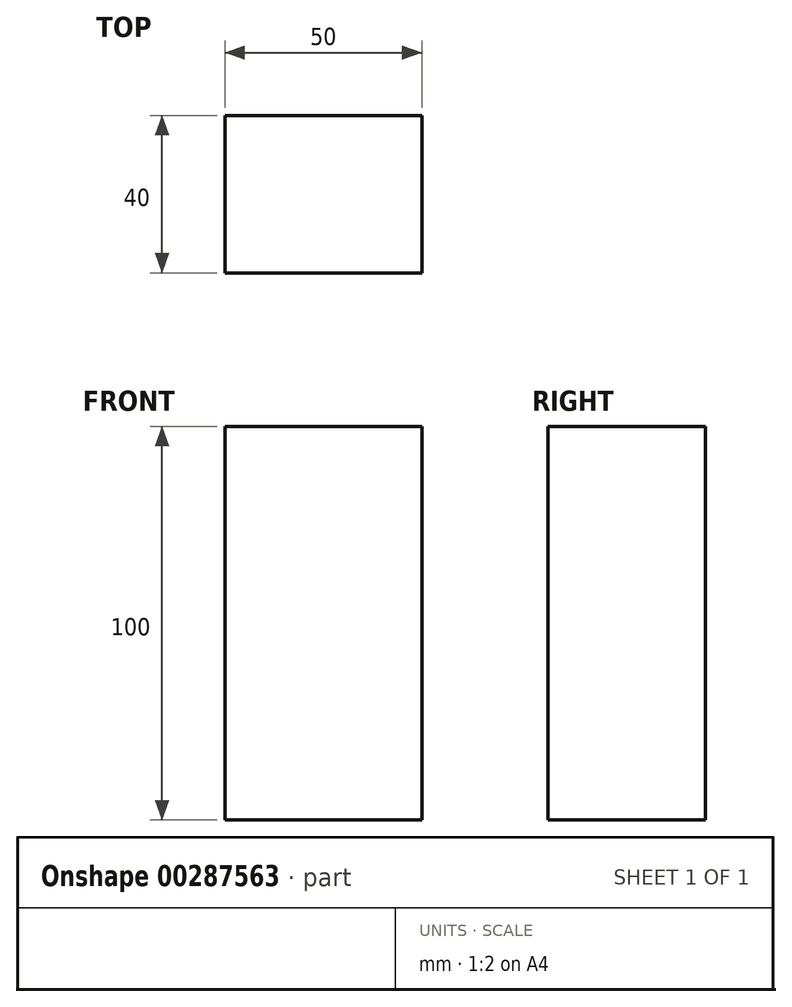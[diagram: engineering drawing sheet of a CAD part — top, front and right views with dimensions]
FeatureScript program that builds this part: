
annotation { "Feature Type Name" : "Feature", "Feature Type Description" : "" }
export const myFeature = defineFeature(function(context is Context, id is Id, definition is map)
    precondition{}
    {
        {
            var Q0;
            Q0=qCreatedBy(makeId("Front.planeOp"),FACE);
            var sketch = newSketch(context, id + "F0", { "sketchPlane" : qUnion([Q0])});
            skLineSegment(sketch, "E0", {"start": v(0, 0) * mm, "end": v(-25, 0) * mm});
            skLineSegment(sketch, "E1", {"start": v(-25, 0) * mm, "end": v(-25, -26.82) * mm});
            skLineSegment(sketch, "E2.bottom", {"start": v(-25, 0) * mm, "end": v(25, 0) * mm});
            skLineSegment(sketch, "E2.top", {"start": v(-25, 100) * mm, "end": v(25, 100) * mm});
            skLineSegment(sketch, "E2.left", {"start": v(-25, 0) * mm, "end": v(-25, 100) * mm});
            skLineSegment(sketch, "E2.right", {"start": v(25, 0) * mm, "end": v(25, 100) * mm});
            skSolve(sketch);
        }
        {
            var Q0;
            Q0 = qSketchRegion(id + "F0", true);
            extrude(context, id + "F1", {"entities" : qUnion([Q0]), "endBound" : BoundingType.SYMMETRIC, "depth" : 40 * mm});
        }
    });
